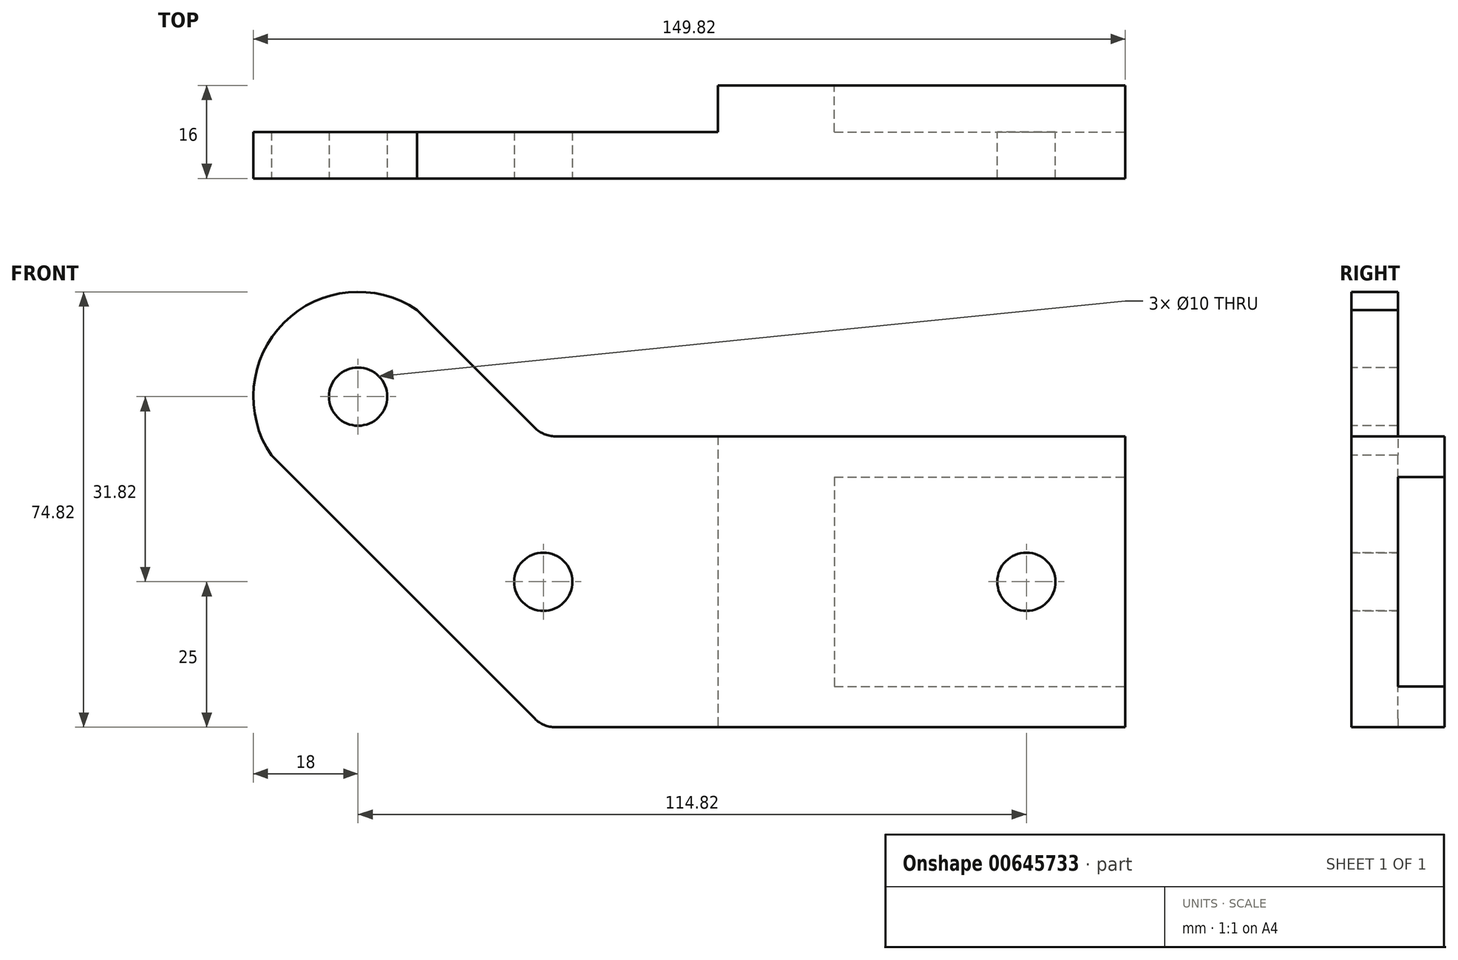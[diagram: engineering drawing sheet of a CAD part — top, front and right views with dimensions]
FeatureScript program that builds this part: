
annotation { "Feature Type Name" : "Feature", "Feature Type Description" : "" }
export const myFeature = defineFeature(function(context is Context, id is Id, definition is map)
    precondition{}
    {
        {
            var Q0;
            Q0=qCreatedBy(makeId("Front.planeOp"),FACE);
            var sketch = newSketch(context, id + "F0", { "sketchPlane" : qUnion([Q0])});
            skLineSegment(sketch, "E0.bottom", {"start": v(-47.93, 0) * mm, "end": v(50, 0) * mm});
            skLineSegment(sketch, "E0.top", {"start": v(-47.93, 50) * mm, "end": v(50, 50) * mm});
            skLineSegment(sketch, "E0.left", {"start": v(-50, 0) * mm, "end": v(-50, 50) * mm, "construction": true});
            skLineSegment(sketch, "E0.right", {"start": v(50, 0) * mm, "end": v(50, 50) * mm});
            skLineSegment(sketch, "E1", {"start": v(-51.46, 1.46) * mm, "end": v(-96.72, 46.72) * mm});
            skLineSegment(sketch, "E2", {"start": v(-51.46, 51.46) * mm, "end": v(-71.72, 71.72) * mm});
            skLineSegment(sketch, "E3.0", {"start": v(-38.55, 13.55) * mm, "end": v(-122.11, 97.11) * mm, "construction": true});
            skCircle(sketch, "E4", {"center": v(-50, 25) * mm, "radius": 5 * mm});
            skCircle(sketch, "E5", {"center": v(-81.82, 56.82) * mm, "radius": 5 * mm});
            skArc(sketch, "E6", {"start": v(-71.72, 71.72) * mm, "mid": v(-94.55, 69.55) * mm, "end": v(-96.72, 46.72) * mm});
            skPoint(sketch, "E7.visualSharp", {"position": v(-50, 50) * mm});
            skArc(sketch, "E7.filletArc", {"start": v(-51.46, 51.46) * mm, "mid": v(-49.84, 50.38) * mm, "end": v(-47.93, 50) * mm});
            skPoint(sketch, "E8.visualSharp", {"position": v(-50, 0) * mm});
            skArc(sketch, "E8.filletArc", {"start": v(-51.46, 1.46) * mm, "mid": v(-49.84, 0.38) * mm, "end": v(-47.93, 0) * mm});
            skSolve(sketch);
        }
        {
            var Q0;
            Q0=makeQuery(id+"F0.imprint","IMPRINT",FACE,{"disambiguationData":[TD([[makeQuery(id+"F0.imprint","IMPRINT",EDGE,{"derivedFrom":sQuery(id+"F0.wireOp",EDGE,"E0.bottom")}),1.0]])]});
            extrude(context, id + "F1", {"entities" : qUnion([Q0]), "oppositeDirection" : true, "depth" : 8 * mm, "offsetDistance" : 25 * mm});
        }
        {
            var Q0;
            Q0=makeQuery(id+"F1.opExtrude","CAP_FACE",FACE,{"disambiguationData":[OSD([sQuery(id+"F0.wireOp",EDGE,"E0.bottom"),sQuery(id+"F0.wireOp",EDGE,"E0.top"),sQuery(id+"F0.wireOp",EDGE,"E0.right"),sQuery(id+"F0.wireOp",EDGE,"E1"),sQuery(id+"F0.wireOp",EDGE,"E2"),sQuery(id+"F0.wireOp",EDGE,"E4"),sQuery(id+"F0.wireOp",EDGE,"E5"),sQuery(id+"F0.wireOp",EDGE,"E6"),sQuery(id+"F0.wireOp",EDGE,"E7.filletArc"),sQuery(id+"F0.wireOp",EDGE,"E8.filletArc")])],"isStart":false});
            var sketch = newSketch(context, id + "F2", { "sketchPlane" : qUnion([Q0])});
            skLineSegment(sketch, "E9.bottom", {"start": v(-50, 50) * mm, "end": v(20, 50) * mm});
            skLineSegment(sketch, "E9.top", {"start": v(-50, 0) * mm, "end": v(20, 0) * mm});
            skLineSegment(sketch, "E9.left", {"start": v(-50, 50) * mm, "end": v(-50, 0) * mm});
            skLineSegment(sketch, "E9.right", {"start": v(20, 50) * mm, "end": v(20, 0) * mm});
            skSolve(sketch);
        }
        {
            var Q0;
            Q0=makeQuery(id+"F2.imprint","IMPRINT",FACE,{"disambiguationData":[TD([[makeQuery(id+"F2.imprint","IMPRINT",EDGE,{"derivedFrom":sQuery(id+"F2.wireOp",EDGE,"E9.bottom")}),1.0]])]});
            extrude(context, id + "F3", {"entities" : qUnion([Q0]), "operationType" : NewBodyOperationType.ADD, "depth" : 8 * mm, "offsetDistance" : 25 * mm});
        }
        {
            var Q0;
            Q0=makeQuery(id+"F3.opExtrude","CAP_FACE",FACE,{"disambiguationData":[OSD([sQuery(id+"F2.wireOp",EDGE,"E9.bottom"),sQuery(id+"F2.wireOp",EDGE,"E9.top"),sQuery(id+"F2.wireOp",EDGE,"E9.left"),sQuery(id+"F2.wireOp",EDGE,"E9.right")])],"isStart":false});
            var sketch = newSketch(context, id + "F4", { "sketchPlane" : qUnion([Q0])});
            skLineSegment(sketch, "E10.bottom", {"start": v(0, 43) * mm, "end": v(-50, 43) * mm});
            skLineSegment(sketch, "E10.top", {"start": v(0, 7) * mm, "end": v(-50, 7) * mm});
            skLineSegment(sketch, "E10.left", {"start": v(0, 43) * mm, "end": v(0, 7) * mm});
            skLineSegment(sketch, "E10.right", {"start": v(-50, 43) * mm, "end": v(-50, 7) * mm});
            skPoint(sketch, "E10.middle", {"position": v(-25, 25) * mm});
            skPoint(sketch, "E10.middle.positionSnap0", {"position": v(-50, 25) * mm});
            skPoint(sketch, "E10.centerSnap0", {"position": v(-50, 25) * mm});
            skSolve(sketch);
        }
        {
            var Q0;
            Q0=makeQuery(id+"F4.imprint","IMPRINT",FACE,{"disambiguationData":[TD([[makeQuery(id+"F4.imprint","IMPRINT",EDGE,{"derivedFrom":sQuery(id+"F4.wireOp",EDGE,"E10.bottom")}),1.0]])]});
            extrude(context, id + "F5", {"entities" : qUnion([Q0]), "operationType" : NewBodyOperationType.REMOVE, "oppositeDirection" : true, "depth" : 8 * mm, "offsetDistance" : 25 * mm});
        }
        {
            var Q0;
            Q0=makeQuery(id+"F5.boolean.opBoolean","COPY",FACE,{"derivedFrom":makeQuery(id+"F5.opExtrude","CAP_FACE",FACE,{"disambiguationData":[OSD([sQuery(id+"F4.wireOp",EDGE,"E10.bottom"),sQuery(id+"F4.wireOp",EDGE,"E10.top"),sQuery(id+"F4.wireOp",EDGE,"E10.left"),sQuery(id+"F4.wireOp",EDGE,"E10.right")])],"isStart":false})});
            var sketch = newSketch(context, id + "F6", { "sketchPlane" : qUnion([Q0])});
            skCircle(sketch, "E11", {"center": v(-33, 25) * mm, "radius": 5 * mm});
            skPoint(sketch, "E11.centerSnap0", {"position": v(-50, 25) * mm});
            skSolve(sketch);
        }
        {
            var Q0;
            Q0=makeQuery(id+"F6.imprint","IMPRINT",FACE,{"disambiguationData":[TD([[makeQuery(id+"F6.imprint","IMPRINT",EDGE,{"derivedFrom":sQuery(id+"F6.wireOp",EDGE,"E11")}),1.0]])]});
            extrude(context, id + "F7", {"entities" : qUnion([Q0]), "operationType" : NewBodyOperationType.REMOVE, "oppositeDirection" : true, "depth" : 25 * mm, "offsetDistance" : 25 * mm});
        }
    });
